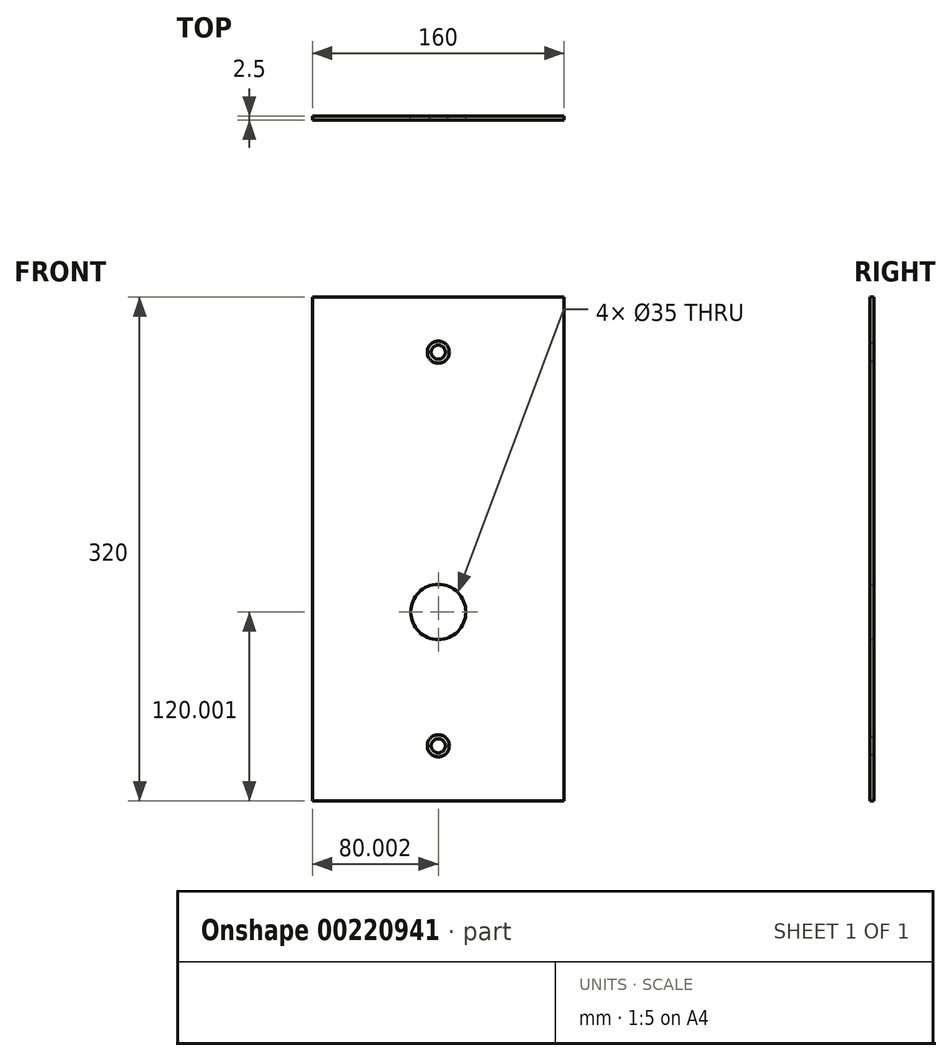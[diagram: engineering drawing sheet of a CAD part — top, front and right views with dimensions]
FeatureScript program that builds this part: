
annotation { "Feature Type Name" : "Feature", "Feature Type Description" : "" }
export const myFeature = defineFeature(function(context is Context, id is Id, definition is map)
    precondition{}
    {
        {
            var Q0;
            Q0=qCreatedBy(makeId("Front.planeOp"),FACE);
            var sketch = newSketch(context, id + "F0", { "sketchPlane" : qUnion([Q0])});
            skLineSegment(sketch, "E0.bottom", {"start": v(-81.89, 189.68) * mm, "end": v(78.11, 189.68) * mm});
            skLineSegment(sketch, "E0.top", {"start": v(-81.89, -130.32) * mm, "end": v(78.11, -130.32) * mm});
            skLineSegment(sketch, "E0.left", {"start": v(-81.89, 189.68) * mm, "end": v(-81.89, -130.32) * mm});
            skLineSegment(sketch, "E0.right", {"start": v(78.11, 189.68) * mm, "end": v(78.11, -130.32) * mm});
            skLineSegment(sketch, "E1", {"start": v(-1.89, 189.68) * mm, "end": v(-1.89, -130.32) * mm, "construction": true});
            skCircle(sketch, "E2", {"center": v(-1.89, 154.68) * mm, "radius": 3 * mm});
            skCircle(sketch, "E3", {"center": v(-1.89, -95.32) * mm, "radius": 3 * mm});
            skCircle(sketch, "E4", {"center": v(-1.89, -10.32) * mm, "radius": 17.5 * mm});
            skSolve(sketch);
        }
        {
            var Q0;
            Q0=makeQuery(id+"F0.imprint","IMPRINT",FACE,{"disambiguationData":[TD([[makeQuery(id+"F0.imprint","IMPRINT",EDGE,{"derivedFrom":sQuery(id+"F0.wireOp",EDGE,"E0.bottom")}),-1.0]])]});
            extrude(context, id + "F1", {"entities" : qUnion([Q0]), "depth" : 2.5 * mm});
        }
        {
            var Q0;
            Q0=makeQuery(id+"F1.opExtrude","CAP_EDGE",EDGE,{"disambiguationData":[OSD([sQuery(id+"F0.wireOp",EDGE,"E2")])],"isStart":false});
            var Q1;
            Q1=makeQuery(id+"F1.opExtrude","CAP_EDGE",EDGE,{"disambiguationData":[OSD([sQuery(id+"F0.wireOp",EDGE,"E3")])],"isStart":false});
            chamfer(context, id + "F2", {"entities" : qUnion([Q0, Q1]), "chamferType" : ChamferType.OFFSET_ANGLE, "width" : 4 * mm, "oppositeDirection" : false, "angle" : 45 * degree, "tangentPropagation" : true});
        }
    });
